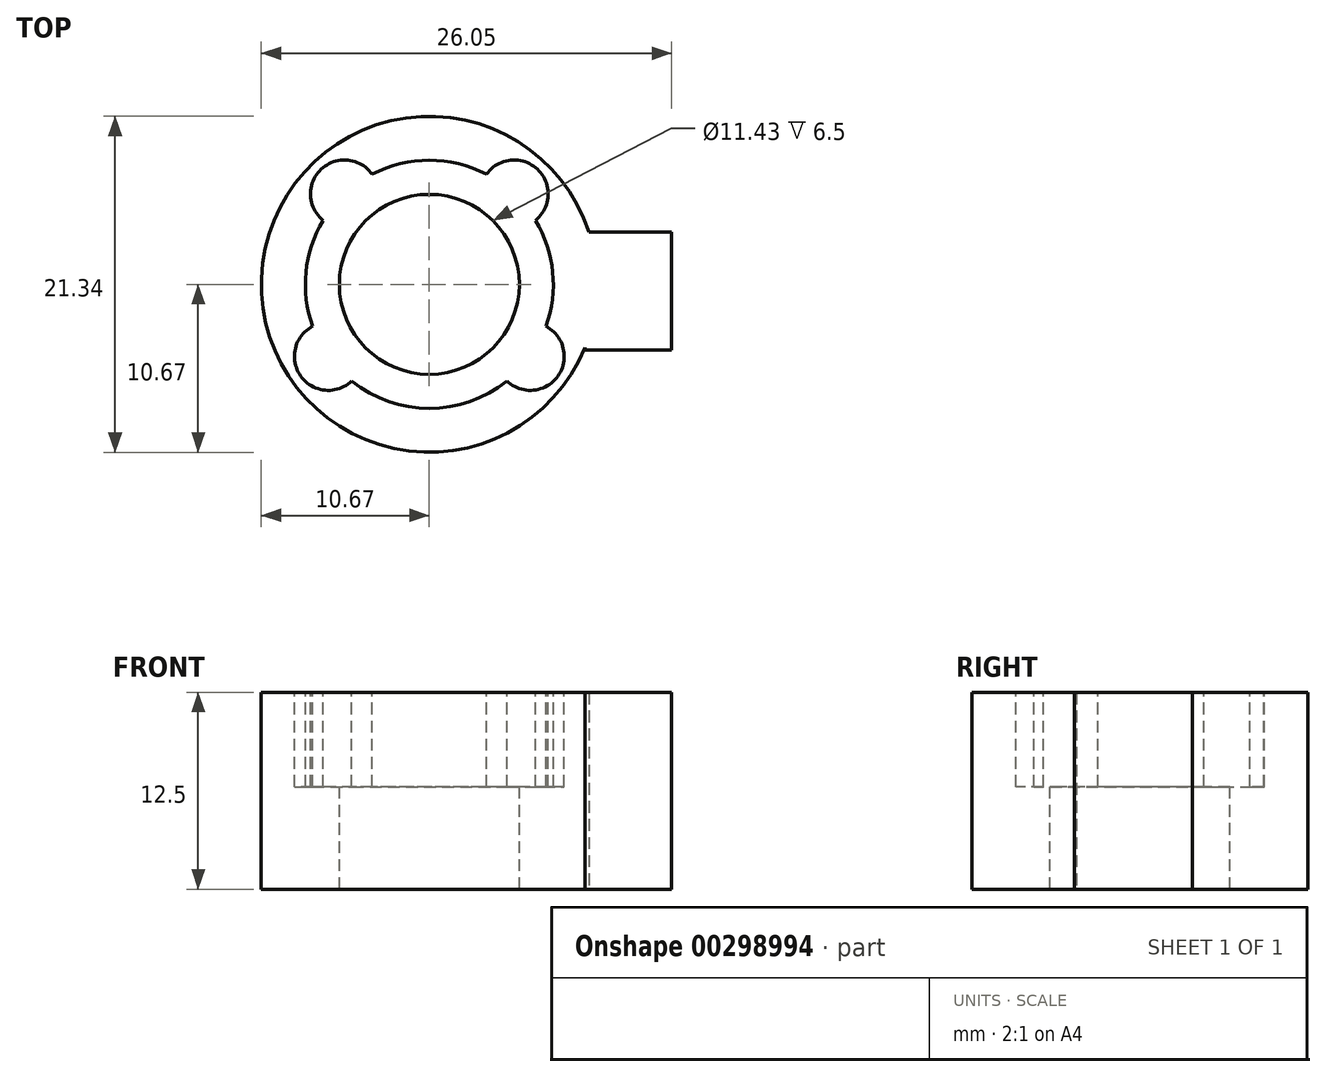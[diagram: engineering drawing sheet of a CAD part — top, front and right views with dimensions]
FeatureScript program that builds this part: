
annotation { "Feature Type Name" : "Feature", "Feature Type Description" : "" }
export const myFeature = defineFeature(function(context is Context, id is Id, definition is map)
    precondition{}
    {
        {
            var Q0;
            Q0=qCreatedBy(makeId("Top.planeOp"),FACE);
            var sketch = newSketch(context, id + "F0", { "sketchPlane" : qUnion([Q0])});
            skCircle(sketch, "E0", {"center": v(0, 0) * mm, "radius": 10.67 * mm});
            skSolve(sketch);
        }
        {
            var Q0;
            Q0 = qSketchRegion(id + "F0", true);
            extrude(context, id + "F1", {"entities" : qUnion([Q0]), "depth" : 12.5 * mm});
        }
        {
            var Q0;
            Q0=makeQuery(id+"F1.opExtrude","CAP_FACE",FACE,{"disambiguationData":[OSD([sQuery(id+"F0.wireOp",EDGE,"E0")])],"isStart":false});
            var sketch = newSketch(context, id + "F2", { "sketchPlane" : qUnion([Q0])});
            skCircle(sketch, "E1", {"center": v(0, 0) * mm, "radius": 7.87 * mm});
            skCircle(sketch, "E2", {"center": v(0, 0) * mm, "radius": 5.72 * mm});
            skCircle(sketch, "E3", {"center": v(-5.4, 5.74) * mm, "radius": 2.16 * mm});
            skCircle(sketch, "E4", {"center": v(5.4, 5.74) * mm, "radius": 2.16 * mm});
            skCircle(sketch, "E5", {"center": v(-6.4, -4.57) * mm, "radius": 2.16 * mm});
            skCircle(sketch, "E6", {"center": v(6.4, -4.57) * mm, "radius": 2.16 * mm});
            skSolve(sketch);
        }
        {
            var Q0;
            Q0 = qSketchRegion(id + "F2", true);
            extrude(context, id + "F3", {"entities" : qUnion([Q0]), "operationType" : NewBodyOperationType.REMOVE, "oppositeDirection" : true, "depth" : 6 * mm});
        }
        {
            var Q0;
            Q0=makeQuery(id+"F3.boolean.opBoolean","SPLIT",FACE,{"disambiguationData":[TD([makeQuery(id+"F3.opExtrude","SWEPT_FACE",FACE,{"disambiguationData":[OSD([sQuery(id+"F2.wireOp",EDGE,"E2")])]})])],"derivedFrom":makeQuery(id+"F1.opExtrude","CAP_FACE",FACE,{"disambiguationData":[OSD([sQuery(id+"F0.wireOp",EDGE,"E0")])],"isStart":false})});
            extrude(context, id + "F4", {"entities" : qUnion([Q0]), "operationType" : NewBodyOperationType.REMOVE, "oppositeDirection" : true, "depth" : 12.5 * mm});
        }
        {
            var Q0;
            Q0=qCreatedBy(makeId("Top.planeOp"),FACE);
            var sketch = newSketch(context, id + "F5", { "sketchPlane" : qUnion([Q0])});
            skLineSegment(sketch, "E7.bottom", {"start": v(9.88, 3.32) * mm, "end": v(15.38, 3.32) * mm});
            skLineSegment(sketch, "E7.top", {"start": v(9.88, -4.18) * mm, "end": v(15.38, -4.18) * mm});
            skLineSegment(sketch, "E7.left", {"start": v(9.88, 3.32) * mm, "end": v(9.88, -4.18) * mm});
            skLineSegment(sketch, "E7.right", {"start": v(15.38, 3.32) * mm, "end": v(15.38, -4.18) * mm});
            skSolve(sketch);
        }
        {
            var Q0;
            Q0 = qSketchRegion(id + "F5", true);
            extrude(context, id + "F6", {"entities" : qUnion([Q0]), "operationType" : NewBodyOperationType.ADD, "depth" : 12.5 * mm});
        }
    });
